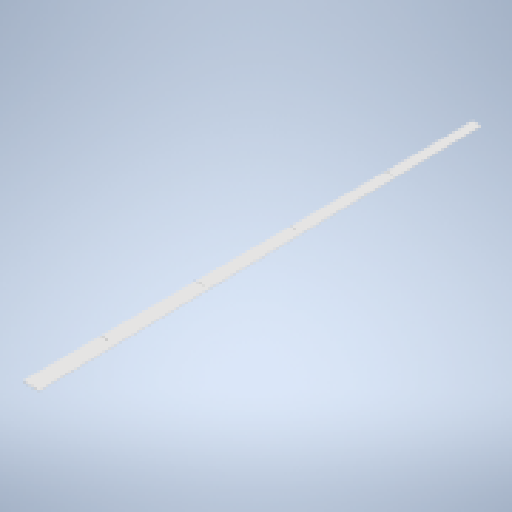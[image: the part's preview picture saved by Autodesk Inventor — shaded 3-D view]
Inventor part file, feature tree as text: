
AUTODESK INVENTOR PART (.ipt)
format: ipt  version: 2025 (Build 290162010, 162A)  size: 642,048 bytes
history: native  units: mm
features: other x3, sketch x3, sheet_metal_op x1, extrude x1, projected_geometry x1
ambient origin geometry x8: Origin, YZ Plane, XZ Plane, XY Plane, X Axis, Y Axis, Z Axis, Center Point
bodies: Solid1 (feature_tree)
feature tree (9):
  sheet_metal_op  "Face1"
  extrude  "Extrusion1"  Depth=200.0mm
  other  "Mark1"
  sketch  "Sketch1"  dims[d2=3.0mm]
  other  "Plate1"
  sketch  "Sketch2"  dims[d3=2400.0mm d4=2950.0mm d5=50.0mm d6=100.0mm d7=50.0mm d9=135.0deg d10=950.0mm d11=1150.0mm d12=23.743743mm d13=50.0mm d14=100.0mm d15=212.132034mm d17=55.0mm d18=200.0mm d19=200.0mm d20=200.0mm]
  projected_geometry  "Projected Loop1"
  sketch  "Sketch3"  dims[d26=3.0mm d29=0.0mm d30=0.0mm d34=46.326363mm d36=41.228805mm d39=36.144545mm d42=31.053636mm d43=560.0mm d44=3.2mm d45=560.0mm d46=3.2mm d47=560.0mm d48=3.2mm d49=3.2mm d50=2705.0mm d52=460.0mm d53=50.0mm]
  other  "Definition1"
